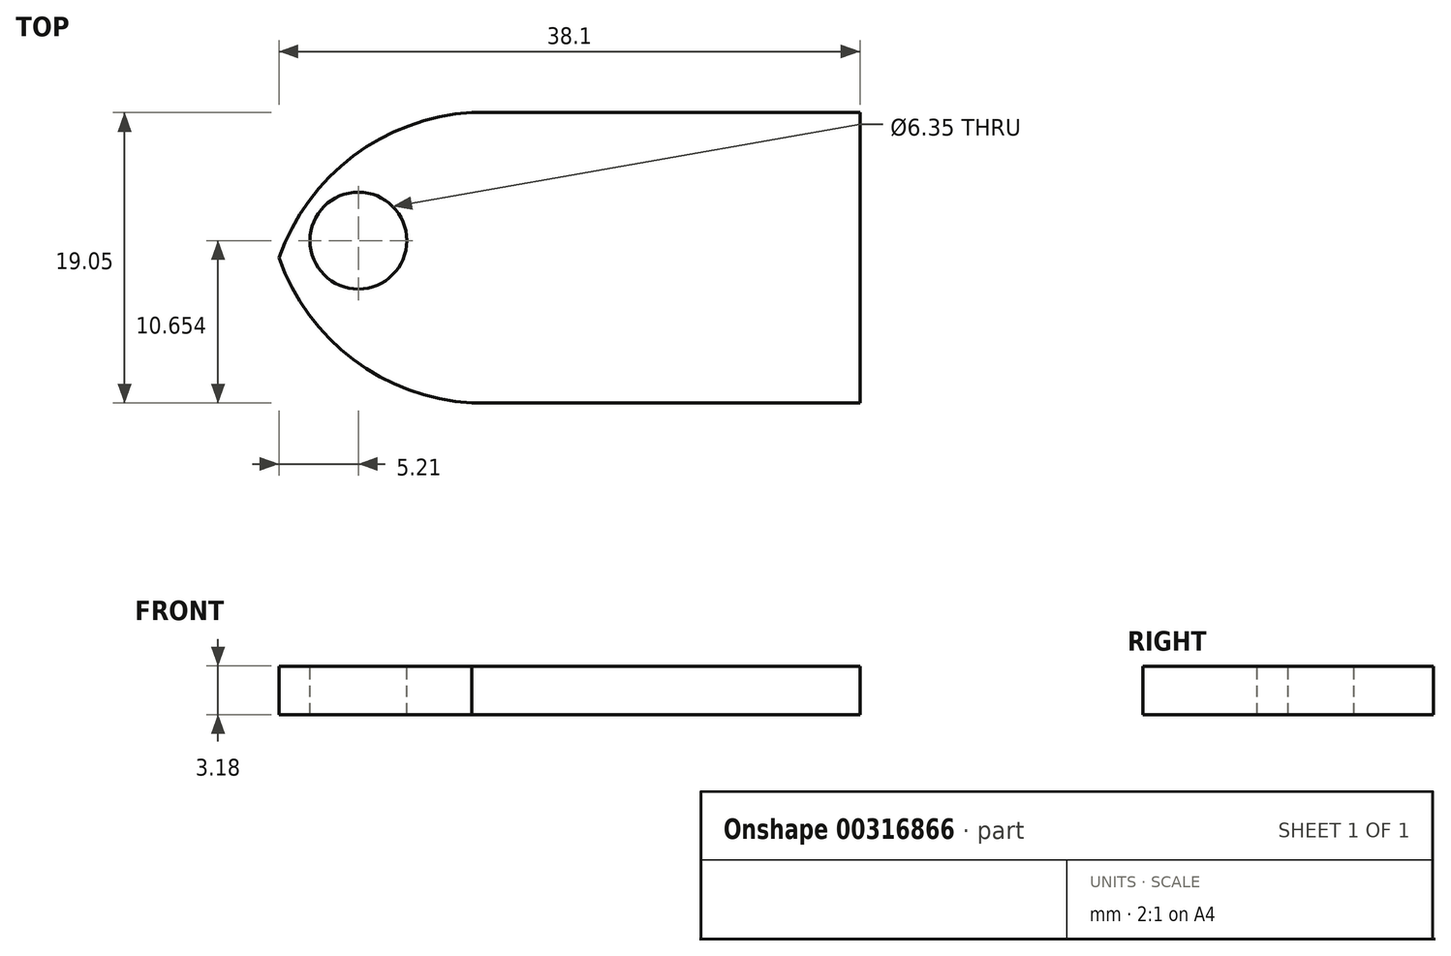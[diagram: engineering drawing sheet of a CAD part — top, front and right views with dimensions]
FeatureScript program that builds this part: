
annotation { "Feature Type Name" : "Feature", "Feature Type Description" : "" }
export const myFeature = defineFeature(function(context is Context, id is Id, definition is map)
    precondition{}
    {
        {
            var Q0;
            Q0=qCreatedBy(makeId("Top.planeOp"),FACE);
            var sketch = newSketch(context, id + "F0", { "sketchPlane" : qUnion([Q0])});
            skLineSegment(sketch, "E0.bottom", {"start": v(0, 0) * mm, "end": v(-38.1, 0) * mm});
            skLineSegment(sketch, "E0.top", {"start": v(0, 19.05) * mm, "end": v(-38.1, 19.05) * mm});
            skLineSegment(sketch, "E0.left", {"start": v(0, 0) * mm, "end": v(0, 19.05) * mm});
            skLineSegment(sketch, "E0.right", {"start": v(-38.1, 0) * mm, "end": v(-38.1, 19.05) * mm});
            skSolve(sketch);
        }
        {
            var Q0;
            Q0 = qSketchRegion(id + "F0", true);
            extrude(context, id + "F1", {"entities" : qUnion([Q0]), "depth" : 3.17 * mm});
        }
        {
            var Q0;
            Q0=makeQuery(id+"F1.opExtrude","CAP_FACE",FACE,{"disambiguationData":[OSD([sQuery(id+"F0.wireOp",EDGE,"E0.bottom"),sQuery(id+"F0.wireOp",EDGE,"E0.top"),sQuery(id+"F0.wireOp",EDGE,"E0.left"),sQuery(id+"F0.wireOp",EDGE,"E0.right")])],"isStart":false});
            var sketch = newSketch(context, id + "F2", { "sketchPlane" : qUnion([Q0])});
            skLineSegment(sketch, "E1", {"start": v(-38.1, 9.52) * mm, "end": v(0, 9.53) * mm, "construction": true});
            skArc(sketch, "E2", {"start": v(-23.76, 19.05) * mm, "mid": v(-32.52, 16.69) * mm, "end": v(-38.1, 9.52) * mm});
            skArc(sketch, "E3.MirrorCS", {"start": v(-23.76, 0) * mm, "mid": v(-32.52, 2.36) * mm, "end": v(-38.1, 9.52) * mm});
            skCircle(sketch, "E4", {"center": v(-33.41, 9.52) * mm, "radius": 1.98 * mm});
            skSolve(sketch);
        }
        {
            var Q0;
            {var subQ1=makeQuery(id+"F1.opExtrude","CAP_EDGE",EDGE,{"disambiguationData":[OSD([sQuery(id+"F0.wireOp",EDGE,"E0.right")])],"isStart":false});var subQ3=makeQuery(id+"F1.opExtrude","CAP_EDGE",EDGE,{"disambiguationData":[OSD([sQuery(id+"F0.wireOp",EDGE,"E0.top")])],"isStart":false});var subQ5=makeQuery(id+"F2.imprint","INTERSECT",VERTEX,{"derivedFrom":[subQ3,subQ1]});Q0=makeQuery(id+"F2.imprint","IMPRINT",FACE,{"disambiguationData":[TD([[makeQuery(id+"F2.imprint","IMPRINT",EDGE,{"disambiguationData":[TD([[subQ5,1.0]])],"derivedFrom":subQ3}),1.0]])]});}
            var Q1;
            {var subQ1=makeQuery(id+"F1.opExtrude","CAP_EDGE",EDGE,{"disambiguationData":[OSD([sQuery(id+"F0.wireOp",EDGE,"E0.right")])],"isStart":false});var subQ3=makeQuery(id+"F1.opExtrude","CAP_EDGE",EDGE,{"disambiguationData":[OSD([sQuery(id+"F0.wireOp",EDGE,"E0.bottom")])],"isStart":false});var subQ5=makeQuery(id+"F2.imprint","INTERSECT",VERTEX,{"derivedFrom":[subQ3,subQ1]});Q1=makeQuery(id+"F2.imprint","IMPRINT",FACE,{"disambiguationData":[TD([[makeQuery(id+"F2.imprint","IMPRINT",EDGE,{"disambiguationData":[TD([[subQ5,1.0]])],"derivedFrom":subQ3}),-1.0]])]});}
            extrude(context, id + "F3", {"entities" : qUnion([Q0, Q1]), "operationType" : NewBodyOperationType.REMOVE, "endBound" : BoundingType.THROUGH_ALL, "oppositeDirection" : true, "depth" : 25.4 * mm});
        }
        {
            var Q0;
            Q0=makeQuery(id+"F1.opExtrude","CAP_FACE",FACE,{"disambiguationData":[OSD([sQuery(id+"F0.wireOp",EDGE,"E0.bottom"),sQuery(id+"F0.wireOp",EDGE,"E0.top"),sQuery(id+"F0.wireOp",EDGE,"E0.left"),sQuery(id+"F0.wireOp",EDGE,"E0.right")])],"isStart":false});
            var sketch = newSketch(context, id + "F4", { "sketchPlane" : qUnion([Q0])});
            skCircle(sketch, "E5", {"center": v(-32.9, 10.65) * mm, "radius": 2.34 * mm});
            skSolve(sketch);
        }
        {
            var Q0;
            Q0=sQuery(id+"F4.wireOp",VERTEX,"E5.center");
            var Q1;
            Q1=makeQuery(id+"F1.opExtrude","SWEPT_BODY",BODY,{"disambiguationData":[OSD([sQuery(id+"F0.wireOp",EDGE,"E0.bottom"),sQuery(id+"F0.wireOp",EDGE,"E0.top"),sQuery(id+"F0.wireOp",EDGE,"E0.left"),sQuery(id+"F0.wireOp",EDGE,"E0.right")])]});
            hole(context, id + "F5", {"style" : HoleStyle.SIMPLE, "endStyle" : HoleEndStyle.THROUGH, "holeDiameter" : 6.35 * mm, "tappedDepth" : 12.7 * mm, "tapClearance" : 3, "locations" : qUnion([Q0]), "scope" : qUnion([Q1])});
        }
    });
